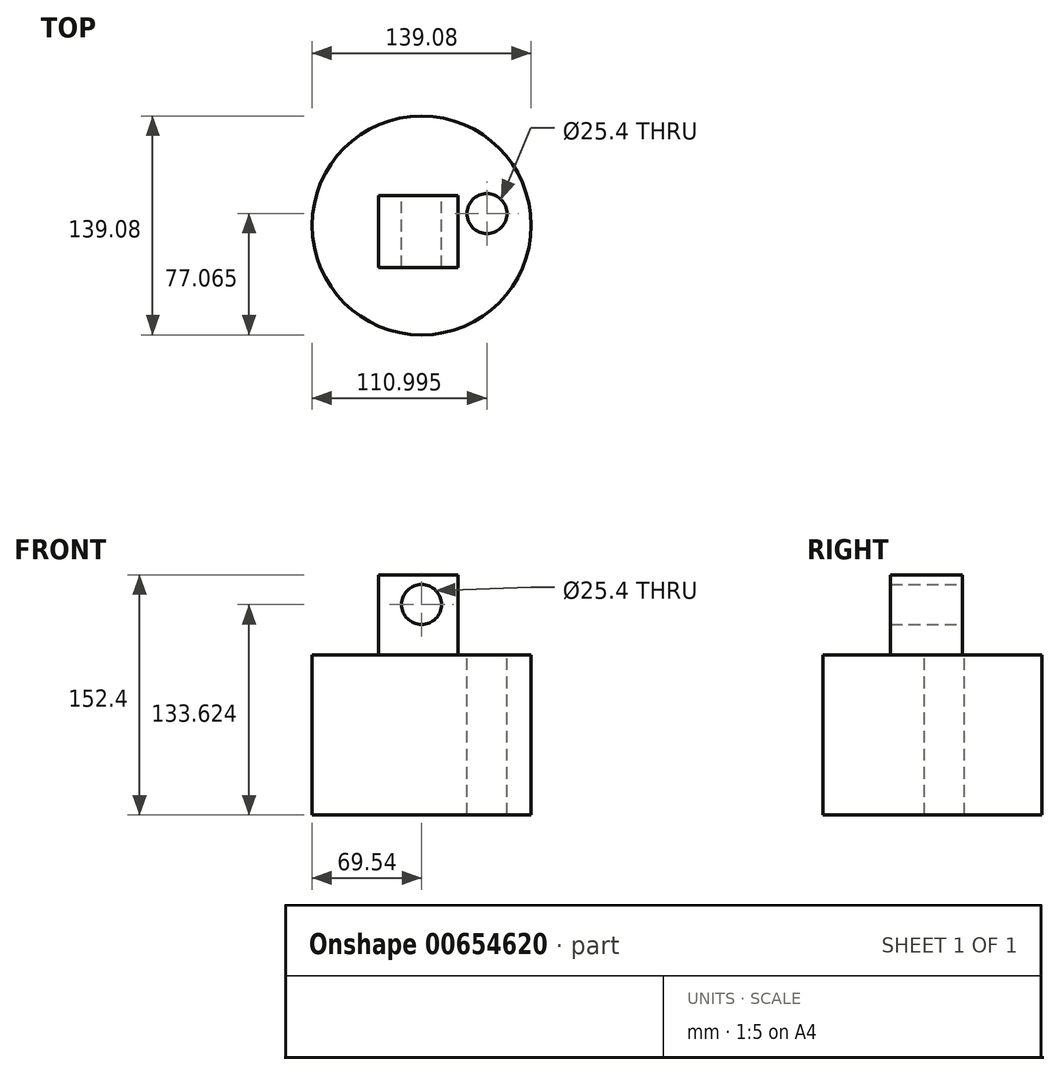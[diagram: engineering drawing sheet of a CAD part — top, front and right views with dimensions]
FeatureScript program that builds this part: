
annotation { "Feature Type Name" : "Feature", "Feature Type Description" : "" }
export const myFeature = defineFeature(function(context is Context, id is Id, definition is map)
    precondition{}
    {
        {
            var Q0;
            Q0=qCreatedBy(makeId("Top.planeOp"),FACE);
            var sketch = newSketch(context, id + "F0", { "sketchPlane" : qUnion([Q0])});
            skCircle(sketch, "E0", {"center": v(0, 0) * mm, "radius": 69.54 * mm});
            skSolve(sketch);
        }
        {
            var Q0;
            Q0=makeQuery(id+"F0.imprint","IMPRINT",FACE,{"disambiguationData":[TD([[makeQuery(id+"F0.imprint","IMPRINT",EDGE,{"derivedFrom":sQuery(id+"F0.wireOp",EDGE,"E0")}),1.0]])]});
            extrude(context, id + "F1", {"entities" : qUnion([Q0]), "depth" : 101.6 * mm, "offsetDistance" : 25.4 * mm});
        }
        {
            var Q0;
            Q0=makeQuery(id+"F1.opExtrude","CAP_FACE",FACE,{"disambiguationData":[OSD([sQuery(id+"F0.wireOp",EDGE,"E0")])],"isStart":false});
            var sketch = newSketch(context, id + "F2", { "sketchPlane" : qUnion([Q0])});
            skLineSegment(sketch, "E1.bottom", {"start": v(23, -26.76) * mm, "end": v(-27.39, -26.76) * mm});
            skLineSegment(sketch, "E1.top", {"start": v(23, 18.9) * mm, "end": v(-27.39, 18.9) * mm});
            skLineSegment(sketch, "E1.left", {"start": v(23, -26.76) * mm, "end": v(23, 18.9) * mm});
            skLineSegment(sketch, "E1.right", {"start": v(-27.39, -26.76) * mm, "end": v(-27.39, 18.9) * mm});
            skSolve(sketch);
        }
        {
            var Q0;
            Q0=makeQuery(id+"F2.imprint","IMPRINT",FACE,{"disambiguationData":[TD([[makeQuery(id+"F2.imprint","IMPRINT",EDGE,{"derivedFrom":sQuery(id+"F2.wireOp",EDGE,"E1.bottom")}),-1.0]])]});
            extrude(context, id + "F3", {"entities" : qUnion([Q0]), "operationType" : NewBodyOperationType.ADD, "depth" : 50.8 * mm, "offsetDistance" : 25.4 * mm});
        }
        {
            var Q0;
            Q0=makeQuery(id+"F3.opExtrude","SWEPT_FACE",FACE,{"disambiguationData":[OSD([sQuery(id+"F2.wireOp",EDGE,"E1.top")])]});
            var sketch = newSketch(context, id + "F4", { "sketchPlane" : qUnion([Q0])});
            skCircle(sketch, "E2", {"center": v(0, 133.62) * mm, "radius": 15.73 * mm});
            skSolve(sketch);
        }
        {
            var Q0;
            Q0=sQuery(id+"F4.wireOp",VERTEX,"E2.center");
            var Q1;
            Q1=makeQuery(id+"F1.opExtrude","SWEPT_BODY",BODY,{"disambiguationData":[OSD([sQuery(id+"F0.wireOp",EDGE,"E0")])]});
            hole(context, id + "F5", {"style" : HoleStyle.SIMPLE, "endStyle" : HoleEndStyle.THROUGH, "holeDiameter" : 25.4 * mm, "majorDiameter" : 6.35 * mm, "isTappedThrough" : true, "tappedDepth" : 12.7 * mm, "tapClearance" : 3, "locations" : qUnion([Q0]), "scope" : qUnion([Q1])});
        }
        {
            var Q0;
            Q0=makeQuery(id+"F1.opExtrude","CAP_FACE",FACE,{"disambiguationData":[OSD([sQuery(id+"F0.wireOp",EDGE,"E0")])],"isStart":false});
            var sketch = newSketch(context, id + "F6", { "sketchPlane" : qUnion([Q0])});
            skCircle(sketch, "E3", {"center": v(41.46, 7.53) * mm, "radius": 12.45 * mm});
            skSolve(sketch);
        }
        {
            var Q0;
            Q0=sQuery(id+"F6.wireOp",VERTEX,"E3.center");
            var Q1;
            Q1=makeQuery(id+"F1.opExtrude","SWEPT_BODY",BODY,{"disambiguationData":[OSD([sQuery(id+"F0.wireOp",EDGE,"E0")])]});
            hole(context, id + "F7", {"style" : HoleStyle.SIMPLE, "endStyle" : HoleEndStyle.THROUGH, "holeDiameter" : 25.4 * mm, "majorDiameter" : 6.35 * mm, "isTappedThrough" : true, "tappedDepth" : 12.7 * mm, "tapClearance" : 3, "locations" : qUnion([Q0]), "scope" : qUnion([Q1])});
        }
    });
